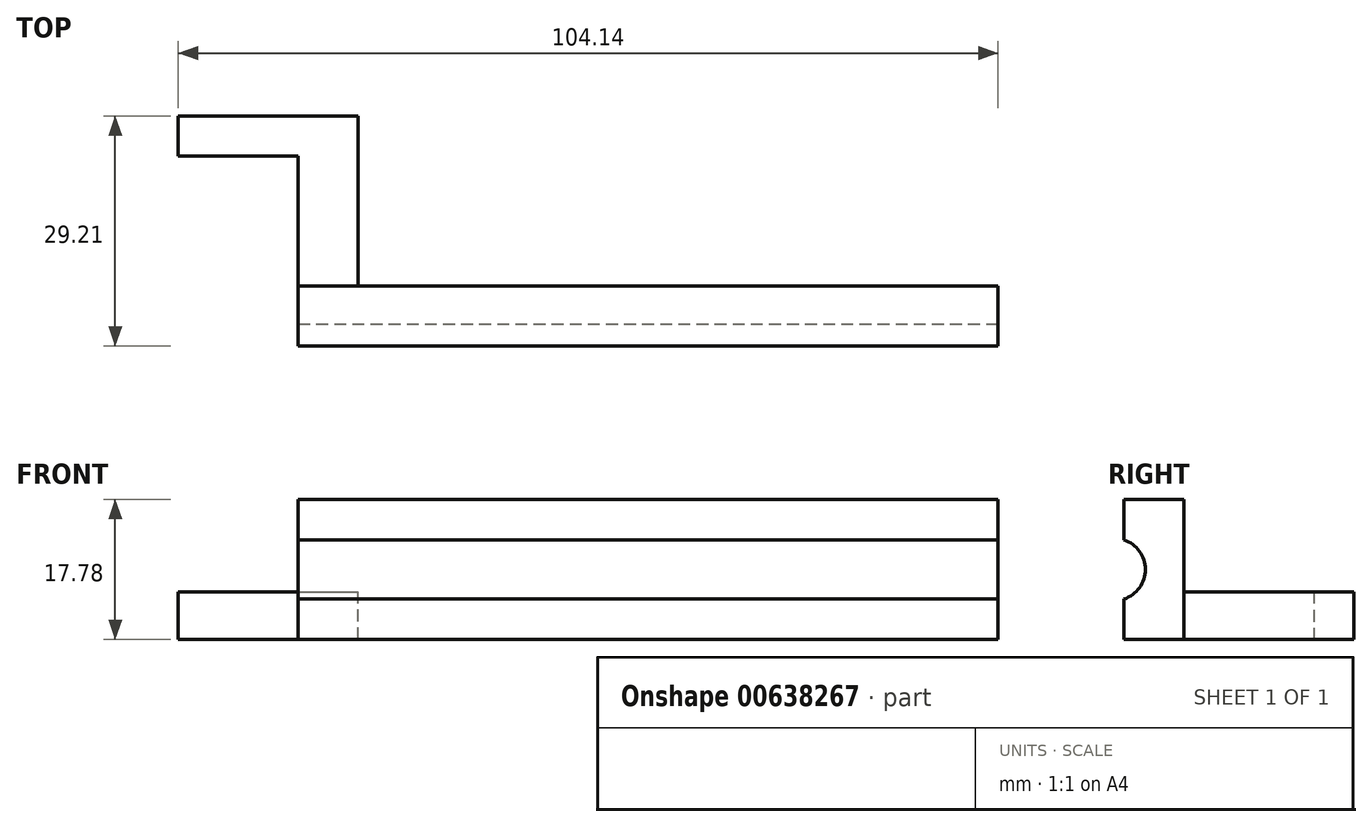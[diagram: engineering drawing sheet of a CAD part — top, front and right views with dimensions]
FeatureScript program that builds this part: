
annotation { "Feature Type Name" : "Feature", "Feature Type Description" : "" }
export const myFeature = defineFeature(function(context is Context, id is Id, definition is map)
    precondition{}
    {
        {
            var Q0;
            Q0=qCreatedBy(makeId("Front.planeOp"),FACE);
            var sketch = newSketch(context, id + "F0", { "sketchPlane" : qUnion([Q0])});
            skLineSegment(sketch, "E0.bottom", {"start": v(0, 0) * mm, "end": v(-88.9, 0) * mm});
            skLineSegment(sketch, "E0.top", {"start": v(0, 17.78) * mm, "end": v(-88.9, 17.78) * mm});
            skLineSegment(sketch, "E0.left", {"start": v(0, 0) * mm, "end": v(0, 17.78) * mm});
            skLineSegment(sketch, "E0.right", {"start": v(-88.9, 0) * mm, "end": v(-88.9, 17.78) * mm});
            skSolve(sketch);
        }
        {
            var Q0;
            Q0=qSketchRegion(id+"F0",true);
            extrude(context, id + "F1", {"entities" : qUnion([Q0]), "depth" : 7.62 * mm, "offsetDistance" : 25.4 * mm});
        }
        {
            var Q0;
            Q0=makeQuery(id+"F1.opExtrude","SWEPT_FACE",FACE,{"disambiguationData":[OSD([sQuery(id+"F0.wireOp",EDGE,"E0.right")])]});
            var sketch = newSketch(context, id + "F2", { "sketchPlane" : qUnion([Q0])});
            skCircle(sketch, "E1", {"center": v(8.9, 8.9) * mm, "radius": 3.98 * mm});
            skSolve(sketch);
        }
        {
            var Q0;
            Q0=qSketchRegion(id+"F2",true);
            extrude(context, id + "F3", {"entities" : qUnion([Q0]), "operationType" : NewBodyOperationType.REMOVE, "endBound" : BoundingType.THROUGH_ALL, "oppositeDirection" : true, "depth" : 25.4 * mm, "offsetDistance" : 25.4 * mm});
        }
        {
            var Q0;
            Q0=makeQuery(id+"F1.opExtrude","CAP_FACE",FACE,{"disambiguationData":[OSD([sQuery(id+"F0.wireOp",EDGE,"E0.bottom"),sQuery(id+"F0.wireOp",EDGE,"E0.top"),sQuery(id+"F0.wireOp",EDGE,"E0.left"),sQuery(id+"F0.wireOp",EDGE,"E0.right")])],"isStart":true});
            var sketch = newSketch(context, id + "F4", { "sketchPlane" : qUnion([Q0])});
            skLineSegment(sketch, "E2.bottom", {"start": v(88.9, 0) * mm, "end": v(81.28, 0) * mm});
            skLineSegment(sketch, "E2.top", {"start": v(88.9, 6.05) * mm, "end": v(81.28, 6.05) * mm});
            skLineSegment(sketch, "E2.left", {"start": v(88.9, 0) * mm, "end": v(88.9, 6.05) * mm});
            skLineSegment(sketch, "E2.right", {"start": v(81.28, 0) * mm, "end": v(81.28, 6.05) * mm});
            skSolve(sketch);
        }
        {
            var Q0;
            Q0 = qSketchRegion(id + "F4", true);
            extrude(context, id + "F5", {"entities" : qUnion([Q0]), "operationType" : NewBodyOperationType.ADD, "depth" : 21.59 * mm, "offsetDistance" : 25.4 * mm});
        }
        {
            var Q0;
            Q0=makeQuery(id+"F5.boolean.opBoolean","MERGE",FACE,{"derivedFrom":[makeQuery(id+"F1.opExtrude","SWEPT_FACE",FACE,{"disambiguationData":[OSD([sQuery(id+"F0.wireOp",EDGE,"E0.right")])]}),makeQuery(id+"F5.opExtrude","SWEPT_FACE",FACE,{"disambiguationData":[OSD([sQuery(id+"F4.wireOp",EDGE,"E2.left")])]})]});
            var sketch = newSketch(context, id + "F6", { "sketchPlane" : qUnion([Q0])});
            skLineSegment(sketch, "E3.bottom", {"start": v(-21.59, 6.05) * mm, "end": v(-16.51, 6.05) * mm});
            skLineSegment(sketch, "E3.top", {"start": v(-21.59, 0) * mm, "end": v(-16.51, 0) * mm});
            skLineSegment(sketch, "E3.left", {"start": v(-21.59, 6.05) * mm, "end": v(-21.59, 0) * mm});
            skLineSegment(sketch, "E3.right", {"start": v(-16.51, 6.05) * mm, "end": v(-16.51, 0) * mm});
            skSolve(sketch);
        }
        {
            var Q0;
            Q0 = qSketchRegion(id + "F6", true);
            extrude(context, id + "F7", {"entities" : qUnion([Q0]), "operationType" : NewBodyOperationType.ADD, "depth" : 15.24 * mm, "offsetDistance" : 25.4 * mm});
        }
    });
